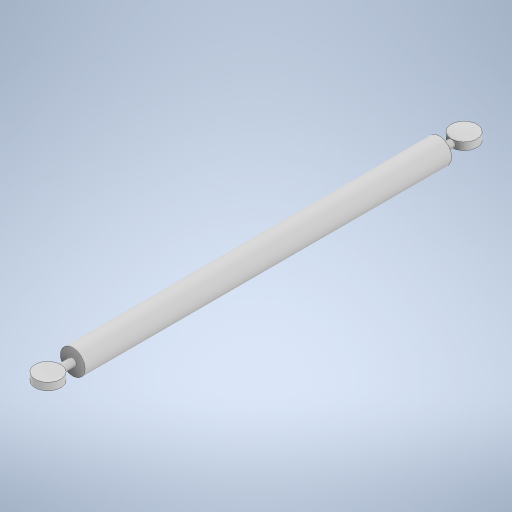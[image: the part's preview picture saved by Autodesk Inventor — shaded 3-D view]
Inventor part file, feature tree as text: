
AUTODESK INVENTOR PART (.ipt)
format: ipt  version: 2023 (Build 270158000, 158)  size: 255,488 bytes
history: native  units: in
note: dims shown in document units (in); Inventor stores cm internally (conversion verified against a paired STEP export)
features: extrude x3, sketch x3, plane x1, mirror x1
ambient origin geometry x8: Origin, YZ Plane, XZ Plane, XY Plane, X Axis, Y Axis, Z Axis, Center Point
bodies: Solid1 (feature_tree)
feature tree (8):
  extrude  "Extrusion1"  Depth=37.0in TaperAngle=0.0deg
  extrude  "Extrusion2"  Depth=0.75in TaperAngle=0.0deg
  extrude  "Extrusion3"  Depth=2.5in
  plane  "Work Plane1"
  mirror  "Mirror1"
  sketch  "Sketch1"  dims[d0=2.5in d1=37.0in d2=0.0in]
  sketch  "Sketch2"  dims[d3=0.75in d4=2.0in d5=0.0in]
  sketch  "Sketch3"  dims[d6=2.6in d7=2.5in d8=0.75in d9=0.0in]
